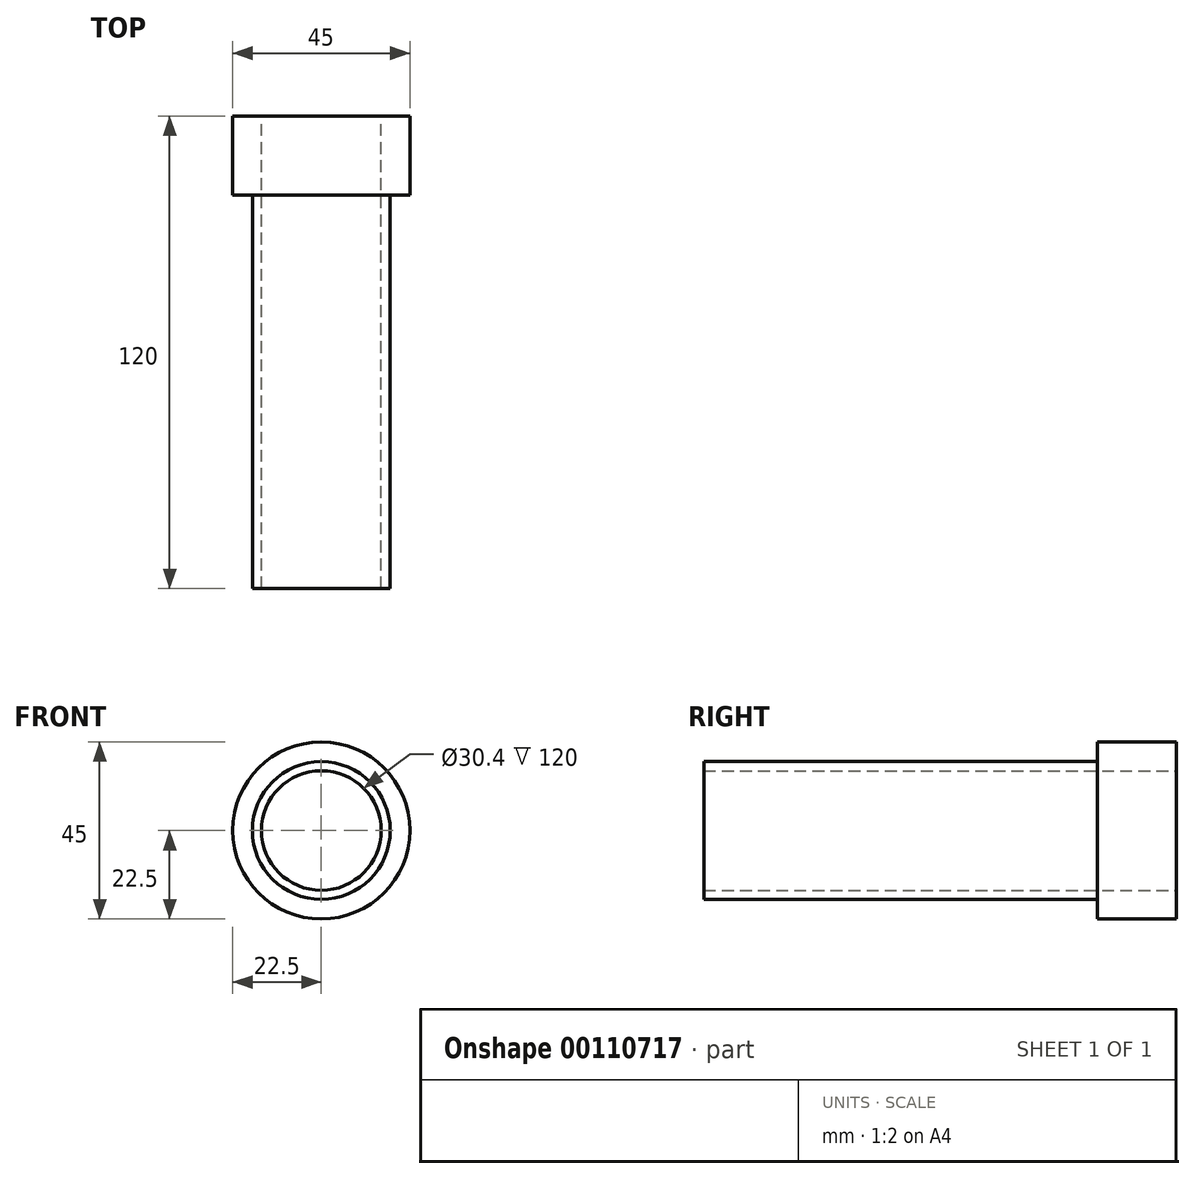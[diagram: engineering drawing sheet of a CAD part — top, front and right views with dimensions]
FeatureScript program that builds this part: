
annotation { "Feature Type Name" : "Feature", "Feature Type Description" : "" }
export const myFeature = defineFeature(function(context is Context, id is Id, definition is map)
    precondition{}
    {
        {
            var Q0;
            Q0=qCreatedBy(makeId("Right.planeOp"),FACE);
            var sketch = newSketch(context, id + "F0", { "sketchPlane" : qUnion([Q0])});
            skLineSegment(sketch, "E0", {"start": v(0, 15.2) * mm, "end": v(-120, 15.2) * mm});
            skLineSegment(sketch, "E1", {"start": v(-120, 15.2) * mm, "end": v(-120, 17.5) * mm});
            skLineSegment(sketch, "E2", {"start": v(-120, 17.5) * mm, "end": v(-20, 17.5) * mm});
            skLineSegment(sketch, "E3", {"start": v(-20, 17.5) * mm, "end": v(-20, 22.5) * mm});
            skLineSegment(sketch, "E4", {"start": v(-20, 22.5) * mm, "end": v(0, 22.5) * mm});
            skLineSegment(sketch, "E5", {"start": v(0, 22.5) * mm, "end": v(0, 15.2) * mm});
            skLineSegment(sketch, "E6", {"start": v(0, 0) * mm, "end": v(-120, 0) * mm, "construction": true});
            skSolve(sketch);
        }
        {
            var Q0;
            Q0 = qSketchRegion(id + "F0", true);
            var Q1;
            Q1=sQuery(id+"F0.wireOp",EDGE,"E6");
            revolve(context, id + "F1", {"entities" : qUnion([Q0]), "axis" : qUnion([Q1]), "revolveType" : RevolveType.FULL});
        }
    });
